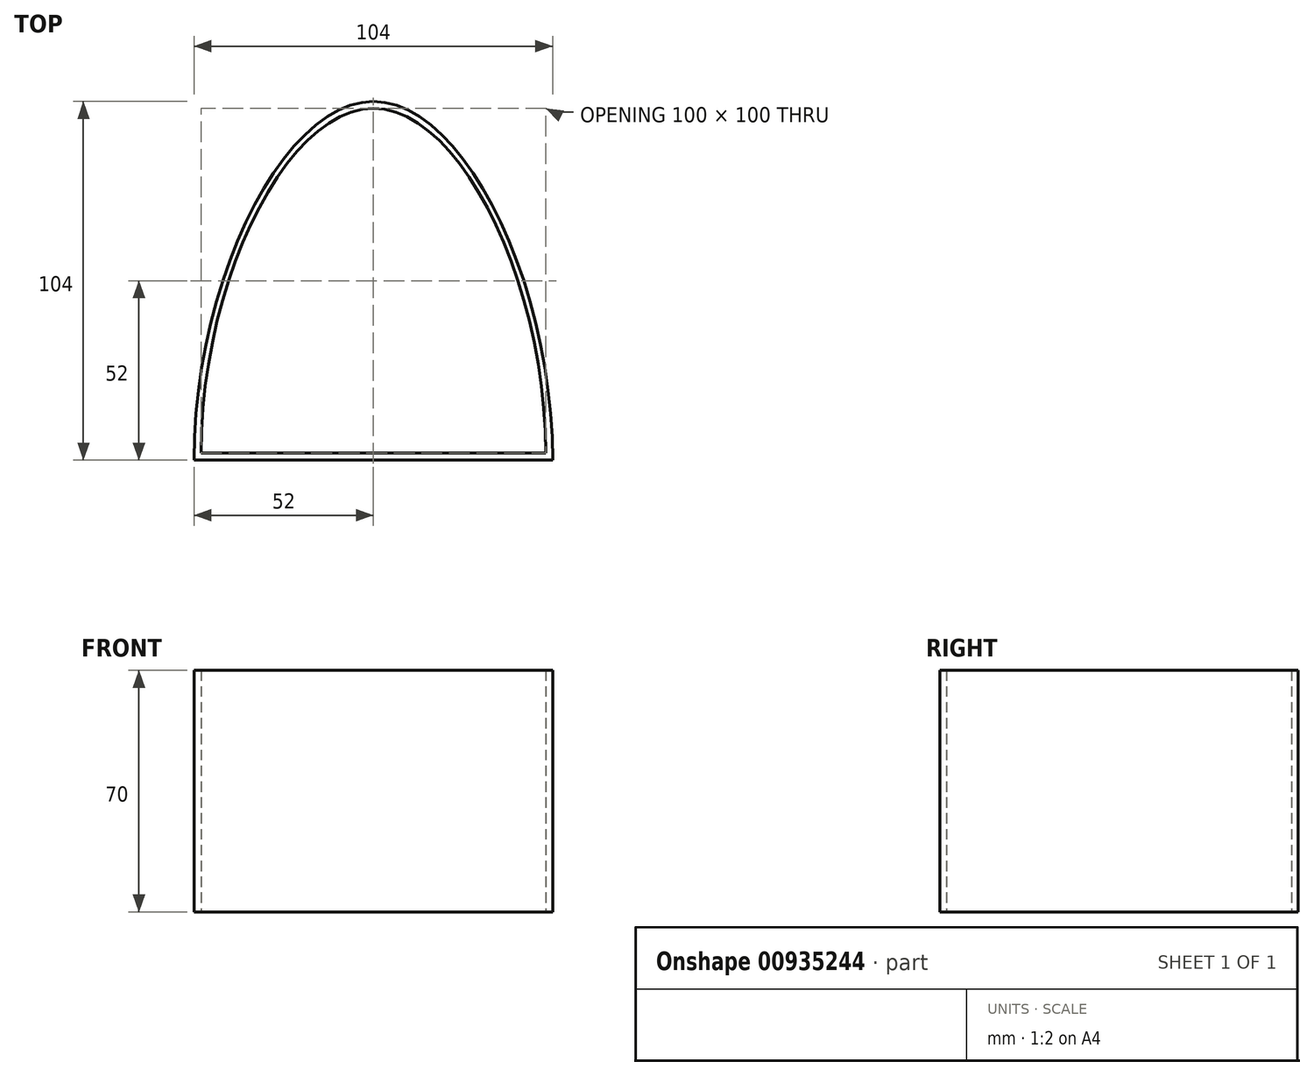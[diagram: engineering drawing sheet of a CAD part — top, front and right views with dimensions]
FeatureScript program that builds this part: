
annotation { "Feature Type Name" : "Feature", "Feature Type Description" : "" }
export const myFeature = defineFeature(function(context is Context, id is Id, definition is map)
    precondition{}
    {
        {
            var Q0;
            Q0=qCreatedBy(makeId("Top.planeOp"),FACE);
            var sketch = newSketch(context, id + "F0", { "sketchPlane" : qUnion([Q0])});
            skLineSegment(sketch, "E0", {"start": v(0, 0) * mm, "end": v(0, 50) * mm});
            skLineSegment(sketch, "E1", {"start": v(0, 0) * mm, "end": v(0, -50) * mm});
            skLineSegment(sketch, "E2", {"start": v(0, -50) * mm, "end": v(50, -50) * mm});
            skLineSegment(sketch, "E3", {"start": v(0, -50) * mm, "end": v(-50, -50) * mm});
            skFitSpline(sketch, "E4", {"points": [v(-50, -50) * mm, v(0, 50) * mm, v(50, -50) * mm], "startDerivative": vector(0, 300) * mm, "endDerivative": vector(0.95, -300) * mm});
            skLineSegment(sketch, "E5", {"start": v(0, -52) * mm, "end": v(-52, -52) * mm});
            skLineSegment(sketch, "E6", {"start": v(0, -52) * mm, "end": v(52, -52) * mm});
            skLineSegment(sketch, "E7", {"start": v(0, -52) * mm, "end": v(0, 52) * mm});
            skFitSpline(sketch, "E8", {"points": [v(-52, -52) * mm, v(0, 52) * mm, v(52, -52) * mm], "startDerivative": vector(0, 312) * mm, "endDerivative": vector(0.95, -312) * mm});
            skSolve(sketch);
        }
        {
            var Q0;
            {var subQ2=sQuery(id+"F0.wireOp",EDGE,"E3");Q0=makeQuery(id+"F0.imprint","IMPRINT",FACE,{"disambiguationData":[TD([[makeQuery(id+"F0.imprint","IMPRINT",EDGE,{"derivedFrom":subQ2}),1.0]])]});}
            var Q1;
            {var subQ1=sQuery(id+"F0.wireOp",EDGE,"E2");Q1=makeQuery(id+"F0.imprint","IMPRINT",FACE,{"disambiguationData":[TD([[makeQuery(id+"F0.imprint","IMPRINT",EDGE,{"derivedFrom":subQ1}),-1.0]])]});}
            extrude(context, id + "F1", {"entities" : qUnion([Q0, Q1]), "depth" : 70 * mm, "offsetDistance" : 25 * mm});
        }
    });
